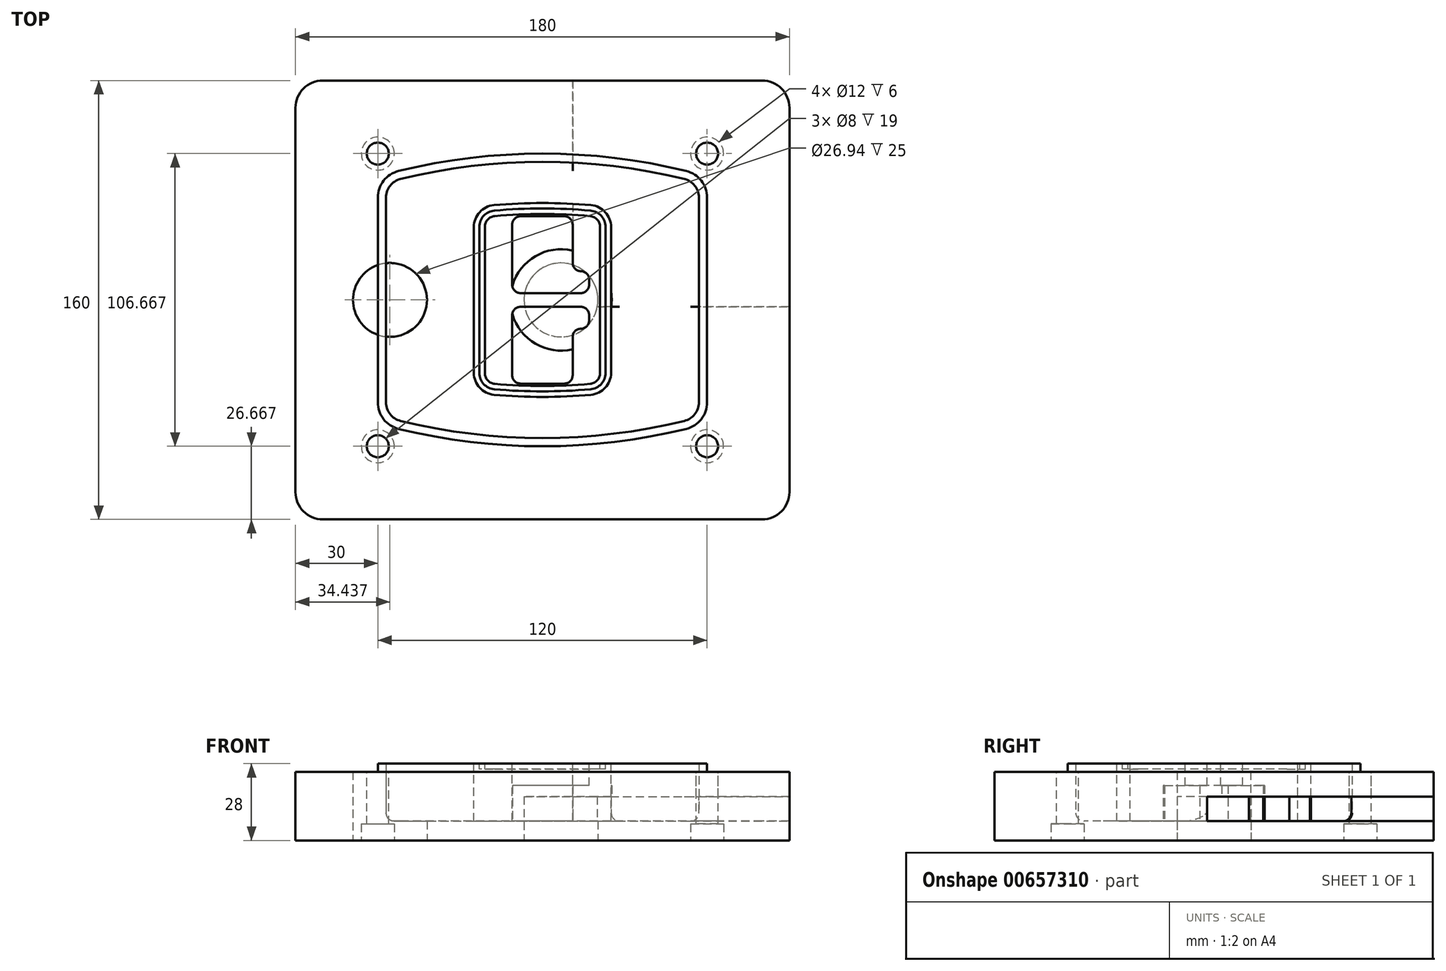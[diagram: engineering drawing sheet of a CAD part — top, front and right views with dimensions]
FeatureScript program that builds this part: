
annotation { "Feature Type Name" : "Feature", "Feature Type Description" : "" }
export const myFeature = defineFeature(function(context is Context, id is Id, definition is map)
    precondition{}
    {
        {
            var Q0;
            Q0=qCreatedBy(makeId("Top.planeOp"),FACE);
            var sketch = newSketch(context, id + "F0", { "sketchPlane" : qUnion([Q0])});
            skPoint(sketch, "E0.rect.middle", {"position": v(0, 0) * mm});
            skLineSegment(sketch, "E1.bottom", {"start": v(-80, -80) * mm, "end": v(80, -80) * mm});
            skLineSegment(sketch, "E1.top", {"start": v(-80, 80) * mm, "end": v(80, 80) * mm});
            skLineSegment(sketch, "E1.left", {"start": v(-90, -70) * mm, "end": v(-90, 70) * mm});
            skLineSegment(sketch, "E1.right", {"start": v(90, -70) * mm, "end": v(90, 70) * mm});
            skLineSegment(sketch, "E2", {"start": v(-90, 80) * mm, "end": v(90, -80) * mm, "construction": true});
            skLineSegment(sketch, "E3", {"start": v(90, 80) * mm, "end": v(-90, -80) * mm, "construction": true});
            skCircle(sketch, "E4", {"center": v(-60, 53.33) * mm, "radius": 4 * mm});
            skCircle(sketch, "E5", {"center": v(60, 53.33) * mm, "radius": 4 * mm});
            skCircle(sketch, "E6", {"center": v(60, -53.33) * mm, "radius": 4 * mm});
            skCircle(sketch, "E7", {"center": v(-60, -53.33) * mm, "radius": 4 * mm});
            skLineSegment(sketch, "E8", {"start": v(-60, 53.33) * mm, "end": v(60, 53.33) * mm, "construction": true});
            skLineSegment(sketch, "E9", {"start": v(60, 53.33) * mm, "end": v(60, -53.33) * mm, "construction": true});
            skLineSegment(sketch, "E10", {"start": v(60, -53.33) * mm, "end": v(-60, -53.33) * mm, "construction": true});
            skLineSegment(sketch, "E11", {"start": v(-60, -53.33) * mm, "end": v(-60, 53.33) * mm, "construction": true});
            skLineSegment(sketch, "E12", {"start": v(-60, 37.3) * mm, "end": v(-60, -37.3) * mm});
            skLineSegment(sketch, "E13", {"start": v(60, 37.3) * mm, "end": v(60, -37.3) * mm});
            skArc(sketch, "E14", {"start": v(52.38, 47.01) * mm, "mid": v(0, 53.33) * mm, "end": v(-52.38, 47.01) * mm});
            skArc(sketch, "E15", {"start": v(-52.38, -47.01) * mm, "mid": v(0, -53.33) * mm, "end": v(52.38, -47.01) * mm});
            skLineSegment(sketch, "E16", {"start": v(-60, 0) * mm, "end": v(60, 0) * mm, "construction": true});
            skPoint(sketch, "E17.visualSharp", {"position": v(-60, -45) * mm});
            skArc(sketch, "E17.filletArc", {"start": v(-60, -37.3) * mm, "mid": v(-57.87, -43.47) * mm, "end": v(-52.38, -47.01) * mm});
            skPoint(sketch, "E18.visualSharp", {"position": v(-60, 45) * mm});
            skArc(sketch, "E18.filletArc", {"start": v(-52.38, 47.01) * mm, "mid": v(-57.87, 43.47) * mm, "end": v(-60, 37.3) * mm});
            skPoint(sketch, "E19.visualSharp", {"position": v(60, 45) * mm});
            skArc(sketch, "E19.filletArc", {"start": v(60, 37.3) * mm, "mid": v(57.87, 43.47) * mm, "end": v(52.38, 47.01) * mm});
            skPoint(sketch, "E20.visualSharp", {"position": v(60, -45) * mm});
            skArc(sketch, "E20.filletArc", {"start": v(52.38, -47.01) * mm, "mid": v(57.87, -43.47) * mm, "end": v(60, -37.3) * mm});
            skPoint(sketch, "E21.visualSharp", {"position": v(-90, 80) * mm});
            skArc(sketch, "E21.filletArc", {"start": v(-80, 80) * mm, "mid": v(-87.07, 77.07) * mm, "end": v(-90, 70) * mm});
            skPoint(sketch, "E22.visualSharp", {"position": v(90, 80) * mm});
            skArc(sketch, "E22.filletArc", {"start": v(90, 70) * mm, "mid": v(87.07, 77.07) * mm, "end": v(80, 80) * mm});
            skPoint(sketch, "E23.visualSharp", {"position": v(90, -80) * mm});
            skArc(sketch, "E23.filletArc", {"start": v(80, -80) * mm, "mid": v(87.07, -77.07) * mm, "end": v(90, -70) * mm});
            skPoint(sketch, "E24.visualSharp", {"position": v(-90, -80) * mm});
            skArc(sketch, "E24.filletArc", {"start": v(-90, -70) * mm, "mid": v(-87.07, -77.07) * mm, "end": v(-80, -80) * mm});
            skArc(sketch, "E25.0", {"start": v(57, 37.3) * mm, "mid": v(55.5, 41.62) * mm, "end": v(51.67, 44.1) * mm});
            skLineSegment(sketch, "E25.1", {"start": v(57, 37.3) * mm, "end": v(57, -37.3) * mm});
            skArc(sketch, "E25.2", {"start": v(51.67, -44.1) * mm, "mid": v(55.5, -41.62) * mm, "end": v(57, -37.3) * mm});
            skArc(sketch, "E25.3", {"start": v(-51.67, -44.1) * mm, "mid": v(0, -50.33) * mm, "end": v(51.67, -44.1) * mm});
            skArc(sketch, "E25.4", {"start": v(-57, -37.3) * mm, "mid": v(-55.5, -41.62) * mm, "end": v(-51.67, -44.1) * mm});
            skArc(sketch, "E25.5", {"start": v(51.67, 44.1) * mm, "mid": v(0, 50.33) * mm, "end": v(-51.67, 44.1) * mm});
            skLineSegment(sketch, "E25.6", {"start": v(-57, 37.3) * mm, "end": v(-57, -37.3) * mm});
            skArc(sketch, "E25.7", {"start": v(-51.67, 44.1) * mm, "mid": v(-55.5, 41.62) * mm, "end": v(-57, 37.3) * mm});
            skArc(sketch, "E26.0", {"start": v(-53.33, 50.9) * mm, "mid": v(-61.01, 45.94) * mm, "end": v(-64, 37.3) * mm});
            skArc(sketch, "E26.1", {"start": v(53.33, 50.9) * mm, "mid": v(0, 57.33) * mm, "end": v(-53.33, 50.9) * mm});
            skArc(sketch, "E26.2", {"start": v(64, 37.3) * mm, "mid": v(61.01, 45.94) * mm, "end": v(53.33, 50.9) * mm});
            skLineSegment(sketch, "E26.3", {"start": v(64, 37.3) * mm, "end": v(64, -37.3) * mm});
            skArc(sketch, "E26.4", {"start": v(53.33, -50.9) * mm, "mid": v(61.01, -45.94) * mm, "end": v(64, -37.3) * mm});
            skLineSegment(sketch, "E26.5", {"start": v(-64, 37.3) * mm, "end": v(-64, -37.3) * mm});
            skArc(sketch, "E26.6", {"start": v(-53.33, -50.9) * mm, "mid": v(0, -57.33) * mm, "end": v(53.33, -50.9) * mm});
            skArc(sketch, "E26.7", {"start": v(-64, -37.3) * mm, "mid": v(-61.01, -45.94) * mm, "end": v(-53.33, -50.9) * mm});
            skSolve(sketch);
        }
        {
            var Q0;
            Q0=makeQuery(id+"F0.imprint","IMPRINT",FACE,{"disambiguationData":[TD([[makeQuery(id+"F0.imprint","IMPRINT",EDGE,{"derivedFrom":sQuery(id+"F0.wireOp",EDGE,"E1.bottom")}),1.0]])]});
            var Q1;
            Q1=makeQuery(id+"F0.imprint","IMPRINT",FACE,{"disambiguationData":[TD([[makeQuery(id+"F0.imprint","IMPRINT",EDGE,{"derivedFrom":sQuery(id+"F0.wireOp",EDGE,"E12")}),1.0]])]});
            var Q2;
            Q2=makeQuery(id+"F0.imprint","IMPRINT",FACE,{"disambiguationData":[TD([[makeQuery(id+"F0.imprint","IMPRINT",EDGE,{"derivedFrom":sQuery(id+"F0.wireOp",EDGE,"E25.0")}),1.0]])]});
            var Q3;
            Q3=makeQuery(id+"F0.imprint","IMPRINT",FACE,{"disambiguationData":[TD([[makeQuery(id+"F0.imprint","IMPRINT",EDGE,{"derivedFrom":sQuery(id+"F0.wireOp",EDGE,"E12")}),-1.0]])]});
            extrude(context, id + "F1", {"entities" : qUnion([Q0, Q1, Q2, Q3]), "oppositeDirection" : true, "depth" : 25 * mm});
        }
        {
            var Q0;
            Q0=makeQuery(id+"F0.imprint","IMPRINT",FACE,{"disambiguationData":[TD([[makeQuery(id+"F0.imprint","IMPRINT",EDGE,{"derivedFrom":sQuery(id+"F0.wireOp",EDGE,"E12")}),1.0]])]});
            extrude(context, id + "F2", {"entities" : qUnion([Q0]), "operationType" : NewBodyOperationType.ADD, "depth" : 3 * mm});
        }
        {
            var Q0;
            Q0=makeQuery(id+"F0.imprint","IMPRINT",FACE,{"disambiguationData":[TD([[makeQuery(id+"F0.imprint","IMPRINT",EDGE,{"derivedFrom":sQuery(id+"F0.wireOp",EDGE,"E25.0")}),1.0]])]});
            extrude(context, id + "F3", {"entities" : qUnion([Q0]), "operationType" : NewBodyOperationType.REMOVE, "oppositeDirection" : true, "depth" : 18 * mm});
        }
        {
            var Q0;
            Q0=makeQuery(id+"F2.opExtrude","CAP_FACE",FACE,{"disambiguationData":[OSD([sQuery(id+"F0.wireOp",EDGE,"E12"),sQuery(id+"F0.wireOp",EDGE,"E13"),sQuery(id+"F0.wireOp",EDGE,"E14"),sQuery(id+"F0.wireOp",EDGE,"E15"),sQuery(id+"F0.wireOp",EDGE,"E17.filletArc"),sQuery(id+"F0.wireOp",EDGE,"E18.filletArc"),sQuery(id+"F0.wireOp",EDGE,"E19.filletArc"),sQuery(id+"F0.wireOp",EDGE,"E20.filletArc"),sQuery(id+"F0.wireOp",EDGE,"E25.0"),sQuery(id+"F0.wireOp",EDGE,"E25.1"),sQuery(id+"F0.wireOp",EDGE,"E25.2"),sQuery(id+"F0.wireOp",EDGE,"E25.3"),sQuery(id+"F0.wireOp",EDGE,"E25.4"),sQuery(id+"F0.wireOp",EDGE,"E25.5"),sQuery(id+"F0.wireOp",EDGE,"E25.6"),sQuery(id+"F0.wireOp",EDGE,"E25.7")])],"isStart":false});
            var sketch = newSketch(context, id + "F4", { "sketchPlane" : qUnion([Q0])});
            skArc(sketch, "E27.0", {"start": v(-17.7, -34.56) * mm, "mid": v(0, -35.33) * mm, "end": v(17.7, -34.56) * mm});
            skArc(sketch, "E28.0", {"start": v(17.7, 34.56) * mm, "mid": v(0, 35.33) * mm, "end": v(-17.7, 34.56) * mm});
            skLineSegment(sketch, "E29", {"start": v(-25, 26.59) * mm, "end": v(-25, -26.59) * mm});
            skLineSegment(sketch, "E30", {"start": v(25, 26.59) * mm, "end": v(25, -26.59) * mm});
            skLineSegment(sketch, "E31", {"start": v(-25, 33.78) * mm, "end": v(25, 33.78) * mm, "construction": true});
            skLineSegment(sketch, "E32", {"start": v(-25, -33.78) * mm, "end": v(25, -33.78) * mm, "construction": true});
            skPoint(sketch, "E33.visualSharp", {"position": v(-25, 33.78) * mm});
            skArc(sketch, "E33.filletArc", {"start": v(-17.7, 34.56) * mm, "mid": v(-22.9, 32) * mm, "end": v(-25, 26.59) * mm});
            skPoint(sketch, "E34.visualSharp", {"position": v(25, 33.78) * mm});
            skArc(sketch, "E34.filletArc", {"start": v(25, 26.59) * mm, "mid": v(22.9, 32) * mm, "end": v(17.7, 34.56) * mm});
            skPoint(sketch, "E35.visualSharp", {"position": v(25, -33.78) * mm});
            skArc(sketch, "E35.filletArc", {"start": v(17.7, -34.56) * mm, "mid": v(22.9, -32) * mm, "end": v(25, -26.59) * mm});
            skPoint(sketch, "E36.visualSharp", {"position": v(-25, -33.78) * mm});
            skArc(sketch, "E36.filletArc", {"start": v(-25, -26.59) * mm, "mid": v(-22.9, -32) * mm, "end": v(-17.7, -34.56) * mm});
            skArc(sketch, "E37.0", {"start": v(51.67, 44.1) * mm, "mid": v(0, 50.33) * mm, "end": v(-51.67, 44.1) * mm});
            skArc(sketch, "E37.1", {"start": v(-51.67, 44.1) * mm, "mid": v(-55.5, 41.62) * mm, "end": v(-57, 37.3) * mm});
            skLineSegment(sketch, "E37.2", {"start": v(-57, 37.3) * mm, "end": v(-57, -37.3) * mm});
            skArc(sketch, "E37.3", {"start": v(-57, -37.3) * mm, "mid": v(-55.5, -41.62) * mm, "end": v(-51.67, -44.1) * mm});
            skArc(sketch, "E37.4", {"start": v(-51.67, -44.1) * mm, "mid": v(0, -50.33) * mm, "end": v(51.67, -44.1) * mm});
            skArc(sketch, "E37.5", {"start": v(51.67, -44.1) * mm, "mid": v(55.5, -41.62) * mm, "end": v(57, -37.3) * mm});
            skLineSegment(sketch, "E37.6", {"start": v(57, 37.3) * mm, "end": v(57, -37.3) * mm});
            skArc(sketch, "E37.7", {"start": v(57, 37.3) * mm, "mid": v(55.5, 41.62) * mm, "end": v(51.67, 44.1) * mm});
            skLineSegment(sketch, "E38.0", {"start": v(23, 26.59) * mm, "end": v(23, -26.59) * mm});
            skArc(sketch, "E38.1", {"start": v(17.53, -32.56) * mm, "mid": v(21.42, -30.64) * mm, "end": v(23, -26.59) * mm});
            skArc(sketch, "E38.2", {"start": v(-17.53, -32.56) * mm, "mid": v(0, -33.33) * mm, "end": v(17.53, -32.56) * mm});
            skArc(sketch, "E38.3", {"start": v(-23, -26.59) * mm, "mid": v(-21.42, -30.64) * mm, "end": v(-17.53, -32.56) * mm});
            skLineSegment(sketch, "E38.4", {"start": v(-23, 26.59) * mm, "end": v(-23, -26.59) * mm});
            skArc(sketch, "E38.5", {"start": v(23, 26.59) * mm, "mid": v(21.42, 30.64) * mm, "end": v(17.53, 32.56) * mm});
            skArc(sketch, "E38.6", {"start": v(-17.53, 32.56) * mm, "mid": v(-21.42, 30.64) * mm, "end": v(-23, 26.59) * mm});
            skArc(sketch, "E38.7", {"start": v(17.53, 32.56) * mm, "mid": v(0, 33.33) * mm, "end": v(-17.53, 32.56) * mm});
            skArc(sketch, "E39.0", {"start": v(21, 26.59) * mm, "mid": v(19.95, 29.29) * mm, "end": v(17.35, 30.57) * mm});
            skLineSegment(sketch, "E39.1", {"start": v(21, 26.59) * mm, "end": v(21, -26.59) * mm});
            skArc(sketch, "E39.2", {"start": v(17.35, -30.57) * mm, "mid": v(19.95, -29.29) * mm, "end": v(21, -26.59) * mm});
            skArc(sketch, "E39.3", {"start": v(-17.35, -30.57) * mm, "mid": v(0, -31.33) * mm, "end": v(17.35, -30.57) * mm});
            skArc(sketch, "E39.4", {"start": v(-21, -26.59) * mm, "mid": v(-19.95, -29.29) * mm, "end": v(-17.35, -30.57) * mm});
            skArc(sketch, "E39.5", {"start": v(17.35, 30.57) * mm, "mid": v(0, 31.33) * mm, "end": v(-17.35, 30.57) * mm});
            skLineSegment(sketch, "E39.6", {"start": v(-21, 26.59) * mm, "end": v(-21, -26.59) * mm});
            skArc(sketch, "E39.7", {"start": v(-17.35, 30.57) * mm, "mid": v(-19.95, 29.29) * mm, "end": v(-21, 26.59) * mm});
            skLineSegment(sketch, "E40", {"start": v(-25, 0) * mm, "end": v(25, 0) * mm, "construction": true});
            skLineSegment(sketch, "E41", {"start": v(-11, 5.5) * mm, "end": v(-11, 27.5) * mm});
            skLineSegment(sketch, "E42", {"start": v(-8, 30.5) * mm, "end": v(8, 30.5) * mm});
            skLineSegment(sketch, "E43", {"start": v(11, 27.5) * mm, "end": v(11, 13.5) * mm});
            skLineSegment(sketch, "E44", {"start": v(14, 10.5) * mm, "end": v(14, 10.5) * mm});
            skLineSegment(sketch, "E45", {"start": v(17, 7.5) * mm, "end": v(17, 5.5) * mm});
            skLineSegment(sketch, "E46", {"start": v(14, 2.5) * mm, "end": v(-8, 2.5) * mm});
            skPoint(sketch, "E47.visualSharp", {"position": v(-11, 30.5) * mm});
            skArc(sketch, "E47.filletArc", {"start": v(-8, 30.5) * mm, "mid": v(-10.12, 29.62) * mm, "end": v(-11, 27.5) * mm});
            skPoint(sketch, "E48.visualSharp", {"position": v(11, 30.5) * mm});
            skArc(sketch, "E48.filletArc", {"start": v(11, 27.5) * mm, "mid": v(10.12, 29.62) * mm, "end": v(8, 30.5) * mm});
            skPoint(sketch, "E49.visualSharp", {"position": v(11, 10.5) * mm});
            skArc(sketch, "E49.filletArc", {"start": v(11, 13.5) * mm, "mid": v(11.88, 11.38) * mm, "end": v(14, 10.5) * mm});
            skPoint(sketch, "E50.visualSharp", {"position": v(17, 10.5) * mm});
            skArc(sketch, "E50.filletArc", {"start": v(17, 7.5) * mm, "mid": v(16.12, 9.62) * mm, "end": v(14, 10.5) * mm});
            skPoint(sketch, "E51.visualSharp", {"position": v(17, 2.5) * mm});
            skArc(sketch, "E51.filletArc", {"start": v(14, 2.5) * mm, "mid": v(16.12, 3.38) * mm, "end": v(17, 5.5) * mm});
            skPoint(sketch, "E52.visualSharp", {"position": v(-11, 2.5) * mm});
            skArc(sketch, "E52.filletArc", {"start": v(-11, 5.5) * mm, "mid": v(-10.12, 3.38) * mm, "end": v(-8, 2.5) * mm});
            skLineSegment(sketch, "E53.0.MirrorCS", {"start": v(14, -2.5) * mm, "end": v(-8, -2.5) * mm});
            skArc(sketch, "E54.0.MirrorCS", {"start": v(-11, -5.5) * mm, "mid": v(-10.12, -3.38) * mm, "end": v(-8, -2.5) * mm});
            skLineSegment(sketch, "E55.0.MirrorCS", {"start": v(-11, -5.5) * mm, "end": v(-11, -27.5) * mm});
            skArc(sketch, "E56.0.MirrorCS", {"start": v(-8, -30.5) * mm, "mid": v(-10.12, -29.62) * mm, "end": v(-11, -27.5) * mm});
            skLineSegment(sketch, "E57.0.MirrorCS", {"start": v(-8, -30.5) * mm, "end": v(8, -30.5) * mm});
            skArc(sketch, "E58.0.MirrorCS", {"start": v(11, -27.5) * mm, "mid": v(10.12, -29.62) * mm, "end": v(8, -30.5) * mm});
            skLineSegment(sketch, "E59.0.MirrorCS", {"start": v(11, -27.5) * mm, "end": v(11, -13.5) * mm});
            skArc(sketch, "E60.0.MirrorCS", {"start": v(11, -13.5) * mm, "mid": v(11.88, -11.38) * mm, "end": v(14, -10.5) * mm});
            skArc(sketch, "E61.0.MirrorCS", {"start": v(17, -7.5) * mm, "mid": v(16.12, -9.62) * mm, "end": v(14, -10.5) * mm});
            skLineSegment(sketch, "E62.0.MirrorCS", {"start": v(17, -7.5) * mm, "end": v(17, -5.5) * mm});
            skArc(sketch, "E63.0.MirrorCS", {"start": v(14, -2.5) * mm, "mid": v(16.12, -3.38) * mm, "end": v(17, -5.5) * mm});
            skSolve(sketch);
        }
        {
            var Q0;
            Q0=makeQuery(id+"F4.imprint","IMPRINT",FACE,{"disambiguationData":[TD([[makeQuery(id+"F4.imprint","IMPRINT",EDGE,{"derivedFrom":sQuery(id+"F4.wireOp",EDGE,"E27.0")}),1.0]])]});
            var Q1;
            Q1=makeQuery(id+"F4.imprint","IMPRINT",FACE,{"disambiguationData":[TD([[makeQuery(id+"F4.imprint","IMPRINT",EDGE,{"derivedFrom":sQuery(id+"F4.wireOp",EDGE,"E38.0")}),-1.0]])]});
            var Q2;
            Q2=makeQuery(id+"F4.imprint","IMPRINT",FACE,{"disambiguationData":[TD([[makeQuery(id+"F4.imprint","IMPRINT",EDGE,{"derivedFrom":sQuery(id+"F4.wireOp",EDGE,"E39.0")}),1.0]])]});
            extrude(context, id + "F5", {"entities" : qUnion([Q0, Q1, Q2]), "operationType" : NewBodyOperationType.ADD, "endBound" : BoundingType.UP_TO_NEXT, "oppositeDirection" : true, "depth" : 25 * mm});
        }
        {
            var Q0;
            Q0=makeQuery(id+"F4.imprint","IMPRINT",FACE,{"disambiguationData":[TD([[makeQuery(id+"F4.imprint","IMPRINT",EDGE,{"derivedFrom":sQuery(id+"F4.wireOp",EDGE,"E38.0")}),-1.0]])]});
            extrude(context, id + "F6", {"entities" : qUnion([Q0]), "operationType" : NewBodyOperationType.REMOVE, "oppositeDirection" : true, "depth" : 2 * mm});
        }
        {
            var Q0;
            Q0=makeQuery(id+"F1.opExtrude","CAP_FACE",FACE,{"disambiguationData":[OSD([sQuery(id+"F0.wireOp",EDGE,"E1.bottom"),sQuery(id+"F0.wireOp",EDGE,"E1.top"),sQuery(id+"F0.wireOp",EDGE,"E1.left"),sQuery(id+"F0.wireOp",EDGE,"E1.right"),sQuery(id+"F0.wireOp",EDGE,"E4"),sQuery(id+"F0.wireOp",EDGE,"E5"),sQuery(id+"F0.wireOp",EDGE,"E6"),sQuery(id+"F0.wireOp",EDGE,"E7"),sQuery(id+"F0.wireOp",EDGE,"E21.filletArc"),sQuery(id+"F0.wireOp",EDGE,"E22.filletArc"),sQuery(id+"F0.wireOp",EDGE,"E23.filletArc"),sQuery(id+"F0.wireOp",EDGE,"E24.filletArc")])],"isStart":false});
            var sketch = newSketch(context, id + "F7", { "sketchPlane" : qUnion([Q0])});
            skCircle(sketch, "E64", {"center": v(6.76, 0) * mm, "radius": 13.47 * mm});
            skCircle(sketch, "E65", {"center": v(-55.56, 0) * mm, "radius": 13.47 * mm});
            skLineSegment(sketch, "E66", {"start": v(90, 0) * mm, "end": v(-90, 0) * mm});
            skCircle(sketch, "E67", {"center": v(6.76, 0) * mm, "radius": 18.47 * mm});
            skCircle(sketch, "E68", {"center": v(60, -53.33) * mm, "radius": 6 * mm});
            skCircle(sketch, "E69", {"center": v(-60, -53.33) * mm, "radius": 6 * mm});
            skCircle(sketch, "E70", {"center": v(-60, 53.33) * mm, "radius": 6 * mm});
            skCircle(sketch, "E71", {"center": v(60, 53.33) * mm, "radius": 6 * mm});
            skSolve(sketch);
        }
        {
            var Q0;
            {var subQ1=sQuery(id+"F7.wireOp",EDGE,"E66");var subQ4=sQuery(id+"F7.wireOp",EDGE,"E64");var subQ6=makeQuery(id+"F7.imprint","INTERSECT",VERTEX,{"disambiguationData":[OD(0.0)],"derivedFrom":[subQ4,subQ1]});Q0=makeQuery(id+"F7.imprint","IMPRINT",FACE,{"disambiguationData":[TD([[makeQuery(id+"F7.imprint","IMPRINT",EDGE,{"disambiguationData":[TD([[subQ6,-1.0]])],"derivedFrom":subQ4}),-1.0]])]});}
            var Q1;
            {var subQ0=sQuery(id+"F7.wireOp",EDGE,"E66");var subQ1=sQuery(id+"F7.wireOp",EDGE,"E64");var subQ3=makeQuery(id+"F7.imprint","INTERSECT",VERTEX,{"disambiguationData":[OD(0.0)],"derivedFrom":[subQ1,subQ0]});Q1=makeQuery(id+"F7.imprint","IMPRINT",FACE,{"disambiguationData":[TD([[makeQuery(id+"F7.imprint","IMPRINT",EDGE,{"disambiguationData":[TD([[subQ3,-1.0]])],"derivedFrom":subQ1}),1.0]])]});}
            var Q2;
            {var subQ0=sQuery(id+"F7.wireOp",EDGE,"E66");var subQ1=sQuery(id+"F7.wireOp",EDGE,"E64");var subQ3=makeQuery(id+"F7.imprint","INTERSECT",VERTEX,{"disambiguationData":[OD(0.0)],"derivedFrom":[subQ1,subQ0]});Q2=makeQuery(id+"F7.imprint","IMPRINT",FACE,{"disambiguationData":[TD([[makeQuery(id+"F7.imprint","IMPRINT",EDGE,{"disambiguationData":[TD([[subQ3,1.0]])],"derivedFrom":subQ1}),1.0]])]});}
            var Q3;
            {var subQ1=sQuery(id+"F7.wireOp",EDGE,"E66");var subQ4=sQuery(id+"F7.wireOp",EDGE,"E64");var subQ6=makeQuery(id+"F7.imprint","INTERSECT",VERTEX,{"disambiguationData":[OD(0.0)],"derivedFrom":[subQ4,subQ1]});Q3=makeQuery(id+"F7.imprint","IMPRINT",FACE,{"disambiguationData":[TD([[makeQuery(id+"F7.imprint","IMPRINT",EDGE,{"disambiguationData":[TD([[subQ6,1.0]])],"derivedFrom":subQ4}),-1.0]])]});}
            extrude(context, id + "F8", {"entities" : qUnion([Q0, Q1, Q2, Q3]), "operationType" : NewBodyOperationType.ADD, "oppositeDirection" : true, "depth" : 20 * mm});
        }
        {
            var Q0;
            {var subQ0=sQuery(id+"F7.wireOp",EDGE,"E66");var subQ1=sQuery(id+"F7.wireOp",EDGE,"E64");var subQ3=makeQuery(id+"F7.imprint","INTERSECT",VERTEX,{"disambiguationData":[OD(0.0)],"derivedFrom":[subQ1,subQ0]});Q0=makeQuery(id+"F7.imprint","IMPRINT",FACE,{"disambiguationData":[TD([[makeQuery(id+"F7.imprint","IMPRINT",EDGE,{"disambiguationData":[TD([[subQ3,-1.0]])],"derivedFrom":subQ1}),1.0]])]});}
            var Q1;
            {var subQ0=sQuery(id+"F7.wireOp",EDGE,"E66");var subQ1=sQuery(id+"F7.wireOp",EDGE,"E64");var subQ3=makeQuery(id+"F7.imprint","INTERSECT",VERTEX,{"disambiguationData":[OD(0.0)],"derivedFrom":[subQ1,subQ0]});Q1=makeQuery(id+"F7.imprint","IMPRINT",FACE,{"disambiguationData":[TD([[makeQuery(id+"F7.imprint","IMPRINT",EDGE,{"disambiguationData":[TD([[subQ3,1.0]])],"derivedFrom":subQ1}),1.0]])]});}
            extrude(context, id + "F9", {"entities" : qUnion([Q0, Q1]), "operationType" : NewBodyOperationType.REMOVE, "oppositeDirection" : true, "depth" : 16 * mm});
        }
        {
            var Q0;
            {var subQ0=sQuery(id+"F7.wireOp",EDGE,"E66");var subQ1=sQuery(id+"F7.wireOp",EDGE,"E65");var subQ3=makeQuery(id+"F7.imprint","INTERSECT",VERTEX,{"disambiguationData":[OD(0.0)],"derivedFrom":[subQ1,subQ0]});Q0=makeQuery(id+"F7.imprint","IMPRINT",FACE,{"disambiguationData":[TD([[makeQuery(id+"F7.imprint","IMPRINT",EDGE,{"disambiguationData":[TD([[subQ3,-1.0]])],"derivedFrom":subQ1}),1.0]])]});}
            var Q1;
            {var subQ0=sQuery(id+"F7.wireOp",EDGE,"E66");var subQ1=sQuery(id+"F7.wireOp",EDGE,"E65");var subQ3=makeQuery(id+"F7.imprint","INTERSECT",VERTEX,{"disambiguationData":[OD(0.0)],"derivedFrom":[subQ1,subQ0]});Q1=makeQuery(id+"F7.imprint","IMPRINT",FACE,{"disambiguationData":[TD([[makeQuery(id+"F7.imprint","IMPRINT",EDGE,{"disambiguationData":[TD([[subQ3,1.0]])],"derivedFrom":subQ1}),1.0]])]});}
            extrude(context, id + "F10", {"entities" : qUnion([Q0, Q1]), "operationType" : NewBodyOperationType.REMOVE, "oppositeDirection" : true, "depth" : 25 * mm});
        }
        {
            var Q0;
            Q0=makeQuery(id+"F7.imprint","IMPRINT",FACE,{"disambiguationData":[TD([[makeQuery(id+"F7.imprint","IMPRINT",EDGE,{"derivedFrom":sQuery(id+"F7.wireOp",EDGE,"E68")}),1.0]])]});
            var Q1;
            Q1=makeQuery(id+"F7.imprint","IMPRINT",FACE,{"disambiguationData":[TD([[makeQuery(id+"F7.imprint","IMPRINT",EDGE,{"derivedFrom":makeQuery(id+"F1.opExtrude","CAP_EDGE",EDGE,{"disambiguationData":[OSD([sQuery(id+"F0.wireOp",EDGE,"E5")])],"isStart":false})}),-1.0]])]});
            var Q2;
            Q2=makeQuery(id+"F7.imprint","IMPRINT",FACE,{"disambiguationData":[TD([[makeQuery(id+"F7.imprint","IMPRINT",EDGE,{"derivedFrom":sQuery(id+"F7.wireOp",EDGE,"E69")}),1.0]])]});
            var Q3;
            Q3=makeQuery(id+"F7.imprint","IMPRINT",FACE,{"disambiguationData":[TD([[makeQuery(id+"F7.imprint","IMPRINT",EDGE,{"derivedFrom":makeQuery(id+"F1.opExtrude","CAP_EDGE",EDGE,{"disambiguationData":[OSD([sQuery(id+"F0.wireOp",EDGE,"E4")])],"isStart":false})}),-1.0]])]});
            var Q4;
            Q4=makeQuery(id+"F7.imprint","IMPRINT",FACE,{"disambiguationData":[TD([[makeQuery(id+"F7.imprint","IMPRINT",EDGE,{"derivedFrom":sQuery(id+"F7.wireOp",EDGE,"E70")}),1.0]])]});
            var Q5;
            Q5=makeQuery(id+"F7.imprint","IMPRINT",FACE,{"disambiguationData":[TD([[makeQuery(id+"F7.imprint","IMPRINT",EDGE,{"derivedFrom":makeQuery(id+"F1.opExtrude","CAP_EDGE",EDGE,{"disambiguationData":[OSD([sQuery(id+"F0.wireOp",EDGE,"E7")])],"isStart":false})}),-1.0]])]});
            var Q6;
            Q6=makeQuery(id+"F7.imprint","IMPRINT",FACE,{"disambiguationData":[TD([[makeQuery(id+"F7.imprint","IMPRINT",EDGE,{"derivedFrom":sQuery(id+"F7.wireOp",EDGE,"E71")}),1.0]])]});
            var Q7;
            Q7=makeQuery(id+"F7.imprint","IMPRINT",FACE,{"disambiguationData":[TD([[makeQuery(id+"F7.imprint","IMPRINT",EDGE,{"derivedFrom":makeQuery(id+"F1.opExtrude","CAP_EDGE",EDGE,{"disambiguationData":[OSD([sQuery(id+"F0.wireOp",EDGE,"E6")])],"isStart":false})}),-1.0]])]});
            extrude(context, id + "F11", {"entities" : qUnion([Q0, Q1, Q2, Q3, Q4, Q5, Q6, Q7]), "operationType" : NewBodyOperationType.REMOVE, "oppositeDirection" : true, "depth" : 6 * mm});
        }
        {
            var Q0;
            Q0=makeQuery(id+"F9.boolean.opBoolean","COPY",FACE,{"derivedFrom":makeQuery(id+"F9.opExtrude","CAP_FACE",FACE,{"disambiguationData":[OSD([sQuery(id+"F7.wireOp",EDGE,"E64")])],"isStart":false})});
            var sketch = newSketch(context, id + "F12", { "sketchPlane" : qUnion([Q0])});
            skArc(sketch, "E72.0", {"start": v(11, -88.19) * mm, "mid": v(97.1, -83.6) * mm, "end": v(92.5, 2.5) * mm});
            skLineSegment(sketch, "E72.1", {"start": v(11, -17.97) * mm, "end": v(11, -17.97) * mm});
            skLineSegment(sketch, "E73", {"start": v(92.5, -105.13) * mm, "end": v(102.3, -105.13) * mm});
            skLineSegment(sketch, "E74.0", {"start": v(92.5, 2.5) * mm, "end": v(14, 2.5) * mm});
            skArc(sketch, "E74.1", {"start": v(14, 2.5) * mm, "mid": v(16.12, 3.38) * mm, "end": v(17, 5.5) * mm});
            skLineSegment(sketch, "E74.2", {"start": v(17, 7.5) * mm, "end": v(17, 5.5) * mm});
            skArc(sketch, "E74.3", {"start": v(17, 7.5) * mm, "mid": v(16.12, 9.62) * mm, "end": v(14, 10.5) * mm});
            skArc(sketch, "E74.4", {"start": v(11, 13.5) * mm, "mid": v(11.88, 11.38) * mm, "end": v(14, 10.5) * mm});
            skLineSegment(sketch, "E74.5", {"start": v(11, 13.5) * mm, "end": v(11, -88.19) * mm});
            skLineSegment(sketch, "E74.7", {"start": v(92.5, -2.5) * mm, "end": v(14, -2.5) * mm});
            skArc(sketch, "E74.8", {"start": v(14, -2.5) * mm, "mid": v(16.12, -3.38) * mm, "end": v(17, -5.5) * mm});
            skLineSegment(sketch, "E74.9", {"start": v(17, -7.5) * mm, "end": v(17, -5.5) * mm});
            skArc(sketch, "E74.10", {"start": v(17, -7.5) * mm, "mid": v(16.12, -9.62) * mm, "end": v(14, -10.5) * mm});
            skArc(sketch, "E74.11", {"start": v(11, -13.5) * mm, "mid": v(11.88, -11.38) * mm, "end": v(14, -10.5) * mm});
            skLineSegment(sketch, "E74.12", {"start": v(11, -17.97) * mm, "end": v(11, -13.5) * mm});
            skPoint(sketch, "E75.orphan", {"position": v(11, -27.5) * mm});
            skPoint(sketch, "E76.orphan", {"position": v(-8, -2.5) * mm});
            skPoint(sketch, "E77.orphan", {"position": v(-8, 2.5) * mm});
            skPoint(sketch, "E78.orphan", {"position": v(11, 27.5) * mm});
            skSolve(sketch);
        }
        {
            var Q0;
            {var subQ7=sQuery(id+"F12.wireOp",EDGE,"E72.0");var subQ14=sQuery(id+"F12.wireOp",EDGE,"E72.1");var subQ16=sQuery(id+"F12.wireOp",EDGE,"E74.1");var subQ18=sQuery(id+"F12.wireOp",EDGE,"E74.8");Q0=qUnion([makeQuery(id+"F12.imprint","IMPRINT",FACE,{"disambiguationData":[TD([[makeQuery(id+"F12.imprint","IMPRINT",EDGE,{"derivedFrom":subQ7}),1.0]])]}),makeQuery(id+"F12.imprint","IMPRINT",FACE,{"disambiguationData":[TD([[makeQuery(id+"F12.imprint","IMPRINT",EDGE,{"derivedFrom":subQ14}),1.0]])]}),makeQuery(id+"F12.imprint","IMPRINT",FACE,{"disambiguationData":[TD([[makeQuery(id+"F12.imprint","IMPRINT",EDGE,{"derivedFrom":subQ16}),1.0]])]}),makeQuery(id+"F12.imprint","IMPRINT",FACE,{"disambiguationData":[TD([[makeQuery(id+"F12.imprint","IMPRINT",EDGE,{"derivedFrom":subQ18}),-1.0]])]})]);}
            var Q1;
            Q1=makeQuery(id+"F5.boolean.opBoolean","SPLIT",FACE,{"disambiguationData":[TD([makeQuery(id+"F5.opExtrude","SWEPT_FACE",FACE,{"disambiguationData":[OSD([sQuery(id+"F4.wireOp",EDGE,"E41")])]})])],"derivedFrom":makeQuery(id+"F3.boolean.opBoolean","COPY",FACE,{"derivedFrom":makeQuery(id+"F3.opExtrude","CAP_FACE",FACE,{"disambiguationData":[OSD([sQuery(id+"F0.wireOp",EDGE,"E25.0"),sQuery(id+"F0.wireOp",EDGE,"E25.1"),sQuery(id+"F0.wireOp",EDGE,"E25.2"),sQuery(id+"F0.wireOp",EDGE,"E25.3"),sQuery(id+"F0.wireOp",EDGE,"E25.4"),sQuery(id+"F0.wireOp",EDGE,"E25.5"),sQuery(id+"F0.wireOp",EDGE,"E25.6"),sQuery(id+"F0.wireOp",EDGE,"E25.7")])],"isStart":false})})});
            extrude(context, id + "F13", {"entities" : qUnion([Q0]), "operationType" : NewBodyOperationType.REMOVE, "endBound" : BoundingType.UP_TO_SURFACE, "endBoundEntityFace" : qUnion([Q1]), "depth" : 25 * mm});
        }
        {
            var Q0;
            Q0=makeQuery(id+"F3.boolean.opBoolean","COPY",EDGE,{"derivedFrom":makeQuery(id+"F3.opExtrude","CAP_EDGE",EDGE,{"disambiguationData":[OSD([sQuery(id+"F0.wireOp",EDGE,"E25.6")])],"isStart":false})});
            var Q1;
            Q1=makeQuery(id+"F8.boolean.opBoolean","INTERSECT",EDGE,{"derivedFrom":[makeQuery(id+"F5.opExtrude","SWEPT_FACE",FACE,{"disambiguationData":[OSD([sQuery(id+"F4.wireOp",EDGE,"E30")])]}),makeQuery(id+"F8.opExtrude","CAP_FACE",FACE,{"disambiguationData":[OSD([sQuery(id+"F7.wireOp",EDGE,"E67")])],"isStart":false})]});
            var Q2;
            Q2=makeQuery(id+"F8.boolean.opBoolean","INTERSECT",EDGE,{"disambiguationData":[OD(1.0)],"derivedFrom":[makeQuery(id+"F5.opExtrude","SWEPT_FACE",FACE,{"disambiguationData":[OSD([sQuery(id+"F4.wireOp",EDGE,"E30")])]}),makeQuery(id+"F8.opExtrude","SWEPT_FACE",FACE,{"disambiguationData":[OSD([sQuery(id+"F7.wireOp",EDGE,"E67")])]})]});
            var Q3;
            {var subQ0=makeQuery(id+"F3.boolean.opBoolean","COPY",FACE,{"derivedFrom":makeQuery(id+"F3.opExtrude","CAP_FACE",FACE,{"disambiguationData":[OSD([sQuery(id+"F0.wireOp",EDGE,"E25.0"),sQuery(id+"F0.wireOp",EDGE,"E25.1"),sQuery(id+"F0.wireOp",EDGE,"E25.2"),sQuery(id+"F0.wireOp",EDGE,"E25.3"),sQuery(id+"F0.wireOp",EDGE,"E25.4"),sQuery(id+"F0.wireOp",EDGE,"E25.5"),sQuery(id+"F0.wireOp",EDGE,"E25.6"),sQuery(id+"F0.wireOp",EDGE,"E25.7")])],"isStart":false})});var subQ1=sQuery(id+"F4.wireOp",EDGE,"E30");Q3=makeQuery(id+"F8.boolean.opBoolean","SPLIT",EDGE,{"disambiguationData":[TD([makeQuery(id+"F5.opExtrude","SWEPT_FACE",FACE,{"disambiguationData":[OSD([sQuery(id+"F4.wireOp",EDGE,"E35.filletArc")])]})])],"derivedFrom":makeQuery(id+"F5.opExtrude","TWEAK_EDGE",EDGE,{"derivedFrom":[subQ0,makeQuery(id+"F4.imprint","IMPRINT",EDGE,{"derivedFrom":subQ1})]})});}
            var Q4;
            {var subQ0=sQuery(id+"F0.wireOp",EDGE,"E25.0");var subQ1=sQuery(id+"F0.wireOp",EDGE,"E25.1");var subQ2=sQuery(id+"F0.wireOp",EDGE,"E25.2");var subQ3=sQuery(id+"F0.wireOp",EDGE,"E25.3");var subQ4=sQuery(id+"F0.wireOp",EDGE,"E25.4");var subQ5=sQuery(id+"F0.wireOp",EDGE,"E25.5");var subQ6=sQuery(id+"F0.wireOp",EDGE,"E25.6");var subQ7=sQuery(id+"F0.wireOp",EDGE,"E25.7");Q4=makeQuery(id+"F8.boolean.opBoolean","INTERSECT",EDGE,{"derivedFrom":[makeQuery(id+"F5.boolean.opBoolean","SPLIT",FACE,{"disambiguationData":[TD([makeQuery(id+"F2.opExtrude","SWEPT_FACE",FACE,{"disambiguationData":[OSD([subQ0])]})])],"derivedFrom":makeQuery(id+"F3.boolean.opBoolean","COPY",FACE,{"derivedFrom":makeQuery(id+"F3.opExtrude","CAP_FACE",FACE,{"disambiguationData":[OSD([subQ0,subQ1,subQ2,subQ3,subQ4,subQ5,subQ6,subQ7])],"isStart":false})})}),makeQuery(id+"F8.opExtrude","SWEPT_FACE",FACE,{"disambiguationData":[OSD([sQuery(id+"F7.wireOp",EDGE,"E67")])]})]});}
            var Q5;
            Q5=makeQuery(id+"F8.boolean.opBoolean","INTERSECT",EDGE,{"disambiguationData":[OD(0.0)],"derivedFrom":[makeQuery(id+"F5.opExtrude","SWEPT_FACE",FACE,{"disambiguationData":[OSD([sQuery(id+"F4.wireOp",EDGE,"E30")])]}),makeQuery(id+"F8.opExtrude","SWEPT_FACE",FACE,{"disambiguationData":[OSD([sQuery(id+"F7.wireOp",EDGE,"E67")])]})]});
            fillet(context, id + "F14", {"entities" : qUnion([Q0, Q1, Q2, Q3, Q4, Q5]), "radius" : 3 * mm, "tangentPropagation" : true, "allowEdgeOverflow" : false});
        }
    });
